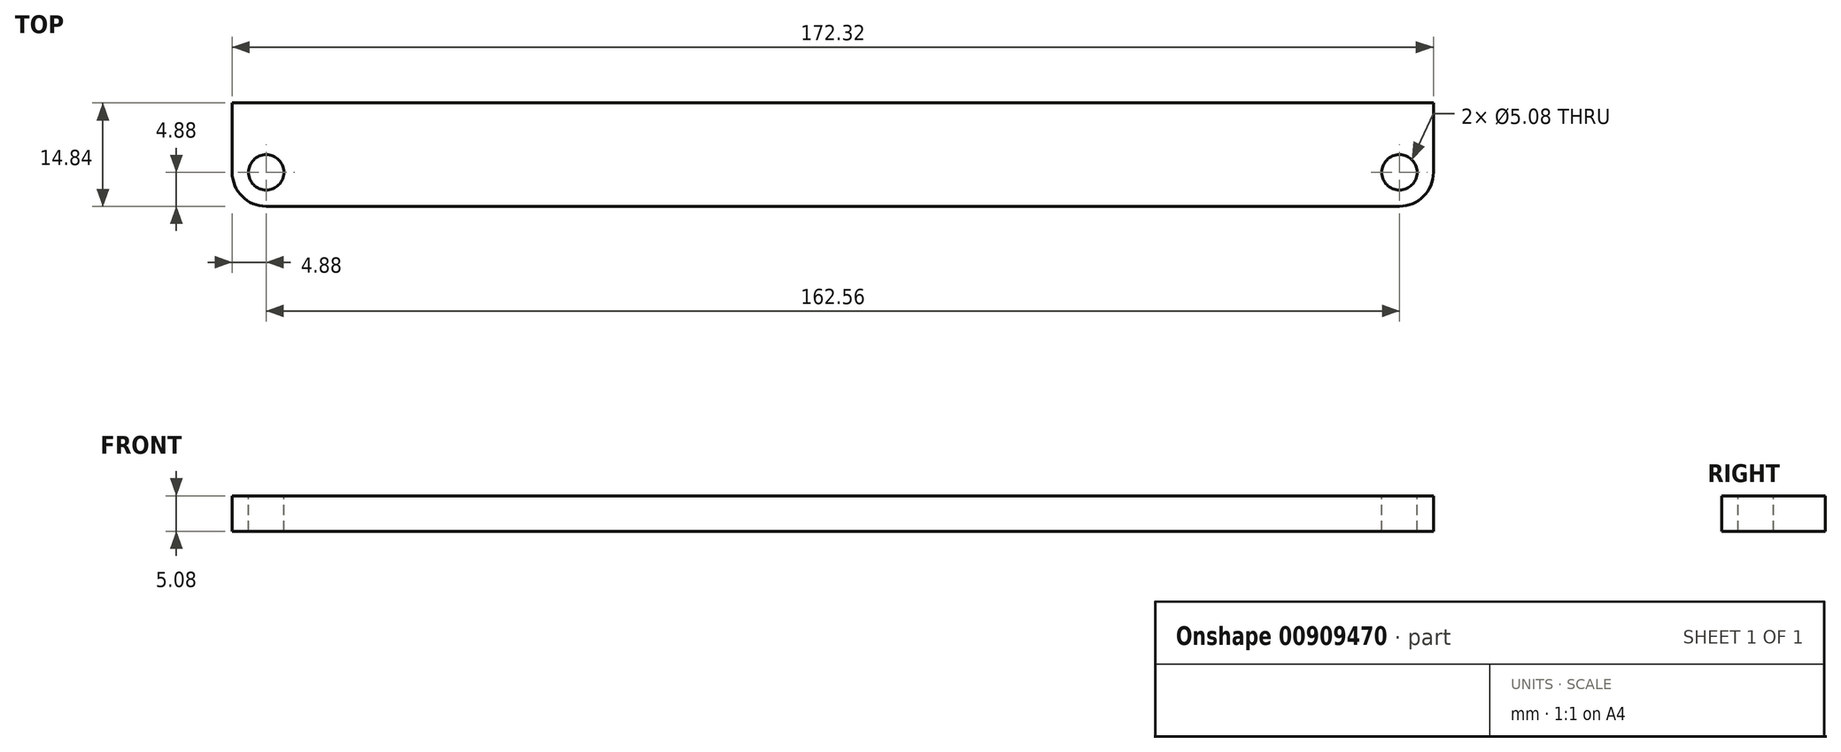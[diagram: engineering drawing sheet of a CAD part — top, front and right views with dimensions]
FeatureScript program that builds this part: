
annotation { "Feature Type Name" : "Feature", "Feature Type Description" : "" }
export const myFeature = defineFeature(function(context is Context, id is Id, definition is map)
    precondition{}
    {
        {
            var Q0;
            Q0=qCreatedBy(makeId("Top.planeOp"),FACE);
            var sketch = newSketch(context, id + "F0", { "sketchPlane" : qUnion([Q0])});
            skLineSegment(sketch, "E0", {"start": v(-86.36, 15.24) * mm, "end": v(-86.36, 5.08) * mm, "construction": true});
            skArc(sketch, "E1", {"start": v(-86.36, 5.08) * mm, "mid": v(-84.87, 1.49) * mm, "end": v(-81.28, 0) * mm, "construction": true});
            skLineSegment(sketch, "E2", {"start": v(86.36, 15.24) * mm, "end": v(86.36, 5.08) * mm, "construction": true});
            skArc(sketch, "E3", {"start": v(81.28, 0) * mm, "mid": v(84.87, 1.49) * mm, "end": v(86.36, 5.08) * mm, "construction": true});
            skLineSegment(sketch, "E4", {"start": v(81.28, 0) * mm, "end": v(-81.28, 0) * mm, "construction": true});
            skLineSegment(sketch, "E5", {"start": v(-86.36, 15.24) * mm, "end": v(86.36, 15.24) * mm, "construction": true});
            skLineSegment(sketch, "E6.0", {"start": v(-86.16, 15.04) * mm, "end": v(-86.16, 5.08) * mm});
            skLineSegment(sketch, "E6.1", {"start": v(86.16, 15.04) * mm, "end": v(86.16, 5.08) * mm});
            skArc(sketch, "E6.2", {"start": v(81.28, 0.2) * mm, "mid": v(84.73, 1.63) * mm, "end": v(86.16, 5.08) * mm});
            skLineSegment(sketch, "E6.3", {"start": v(-86.16, 15.04) * mm, "end": v(86.16, 15.04) * mm});
            skLineSegment(sketch, "E6.4", {"start": v(81.28, 0.2) * mm, "end": v(-81.28, 0.2) * mm});
            skArc(sketch, "E6.5", {"start": v(-86.16, 5.08) * mm, "mid": v(-84.73, 1.63) * mm, "end": v(-81.28, 0.2) * mm});
            skSolve(sketch);
        }
        {
            var Q0;
            Q0 = qSketchRegion(id + "F0", true);
            extrude(context, id + "F1", {"entities" : qUnion([Q0]), "depth" : 5.08 * mm, "offsetDistance" : 25.4 * mm});
        }
        {
            var Q0;
            Q0=makeQuery(id+"F1.opExtrude","CAP_FACE",FACE,{"disambiguationData":[OSD([sQuery(id+"F0.wireOp",EDGE,"E6.0"),sQuery(id+"F0.wireOp",EDGE,"E6.1"),sQuery(id+"F0.wireOp",EDGE,"E6.2"),sQuery(id+"F0.wireOp",EDGE,"E6.3"),sQuery(id+"F0.wireOp",EDGE,"E6.4"),sQuery(id+"F0.wireOp",EDGE,"E6.5")])],"isStart":false});
            var sketch = newSketch(context, id + "F2", { "sketchPlane" : qUnion([Q0])});
            skCircle(sketch, "E7", {"center": v(-81.28, 5.08) * mm, "radius": 2.54 * mm});
            skCircle(sketch, "E8", {"center": v(81.28, 5.08) * mm, "radius": 2.54 * mm});
            skSolve(sketch);
        }
        {
            var Q0;
            Q0 = qSketchRegion(id + "F2", true);
            extrude(context, id + "F3", {"entities" : qUnion([Q0]), "operationType" : NewBodyOperationType.REMOVE, "endBound" : BoundingType.THROUGH_ALL, "oppositeDirection" : true, "depth" : 25.4 * mm, "offsetDistance" : 25.4 * mm});
        }
    });
